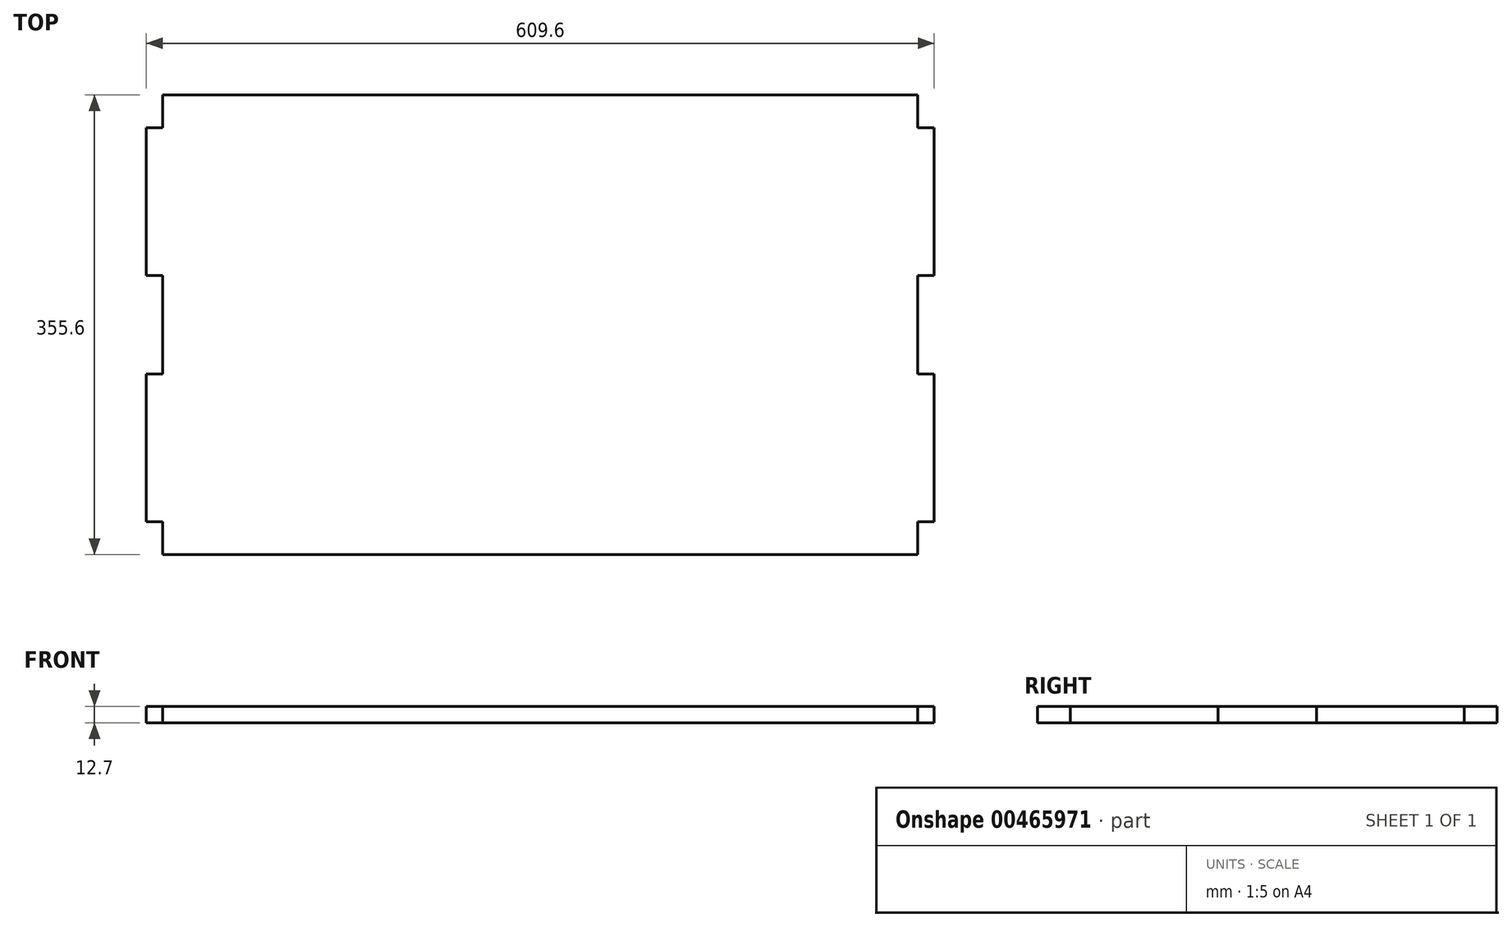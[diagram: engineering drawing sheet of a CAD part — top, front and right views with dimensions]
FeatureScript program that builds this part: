
annotation { "Feature Type Name" : "Feature", "Feature Type Description" : "" }
export const myFeature = defineFeature(function(context is Context, id is Id, definition is map)
    precondition{}
    {
        {
            var Q0;
            Q0=qCreatedBy(makeId("Top.planeOp"),FACE);
            var sketch = newSketch(context, id + "F0", { "sketchPlane" : qUnion([Q0])});
            skLineSegment(sketch, "E0.bottom", {"start": v(-292.1, 177.8) * mm, "end": v(292.1, 177.8) * mm});
            skLineSegment(sketch, "E0.top", {"start": v(-292.1, -177.8) * mm, "end": v(292.1, -177.8) * mm});
            skLineSegment(sketch, "E0.left", {"start": v(-304.8, 152.4) * mm, "end": v(-304.8, 38.1) * mm});
            skLineSegment(sketch, "E0.right", {"start": v(304.8, 152.4) * mm, "end": v(304.8, 38.1) * mm});
            skLineSegment(sketch, "E1", {"start": v(-304.8, -38.1) * mm, "end": v(-292.1, -38.1) * mm});
            skLineSegment(sketch, "E2", {"start": v(-292.1, -38.1) * mm, "end": v(-292.1, 38.1) * mm});
            skLineSegment(sketch, "E3", {"start": v(-292.1, 38.1) * mm, "end": v(-304.8, 38.1) * mm});
            skLineSegment(sketch, "E4", {"start": v(-304.8, 152.4) * mm, "end": v(-292.1, 152.4) * mm});
            skLineSegment(sketch, "E5", {"start": v(-292.1, 152.4) * mm, "end": v(-292.1, 177.8) * mm});
            skLineSegment(sketch, "E6", {"start": v(-292.1, -177.8) * mm, "end": v(-292.1, -152.4) * mm});
            skLineSegment(sketch, "E7", {"start": v(-292.1, -152.4) * mm, "end": v(-304.8, -152.4) * mm});
            skLineSegment(sketch, "E8", {"start": v(304.8, 38.1) * mm, "end": v(292.1, 38.1) * mm});
            skLineSegment(sketch, "E9", {"start": v(292.1, 38.1) * mm, "end": v(292.1, -38.1) * mm});
            skLineSegment(sketch, "E10", {"start": v(292.1, -38.1) * mm, "end": v(304.8, -38.1) * mm});
            skLineSegment(sketch, "E11", {"start": v(304.8, 152.4) * mm, "end": v(292.1, 152.4) * mm});
            skLineSegment(sketch, "E12", {"start": v(292.1, 152.4) * mm, "end": v(292.1, 177.8) * mm});
            skLineSegment(sketch, "E13", {"start": v(304.8, -152.4) * mm, "end": v(292.1, -152.4) * mm});
            skLineSegment(sketch, "E14", {"start": v(292.1, -152.4) * mm, "end": v(292.1, -177.8) * mm});
            skLineSegment(sketch, "E15.trimOffspring", {"start": v(-304.8, -38.1) * mm, "end": v(-304.8, -152.4) * mm});
            skLineSegment(sketch, "E16.trimOffspring", {"start": v(304.8, -38.1) * mm, "end": v(304.8, -152.4) * mm});
            skLineSegment(sketch, "E17", {"start": v(0, 177.8) * mm, "end": v(0, 0) * mm, "construction": true});
            skLineSegment(sketch, "E18", {"start": v(-292.1, 0) * mm, "end": v(0, 0) * mm, "construction": true});
            skSolve(sketch);
        }
        {
            var Q0;
            Q0=makeQuery(id+"F0.imprint","IMPRINT",FACE,{"disambiguationData":[TD([[makeQuery(id+"F0.imprint","IMPRINT",EDGE,{"derivedFrom":sQuery(id+"F0.wireOp",EDGE,"E0.bottom")}),-1.0]])]});
            extrude(context, id + "F1", {"entities" : qUnion([Q0]), "depth" : 12.7 * mm});
        }
    });
